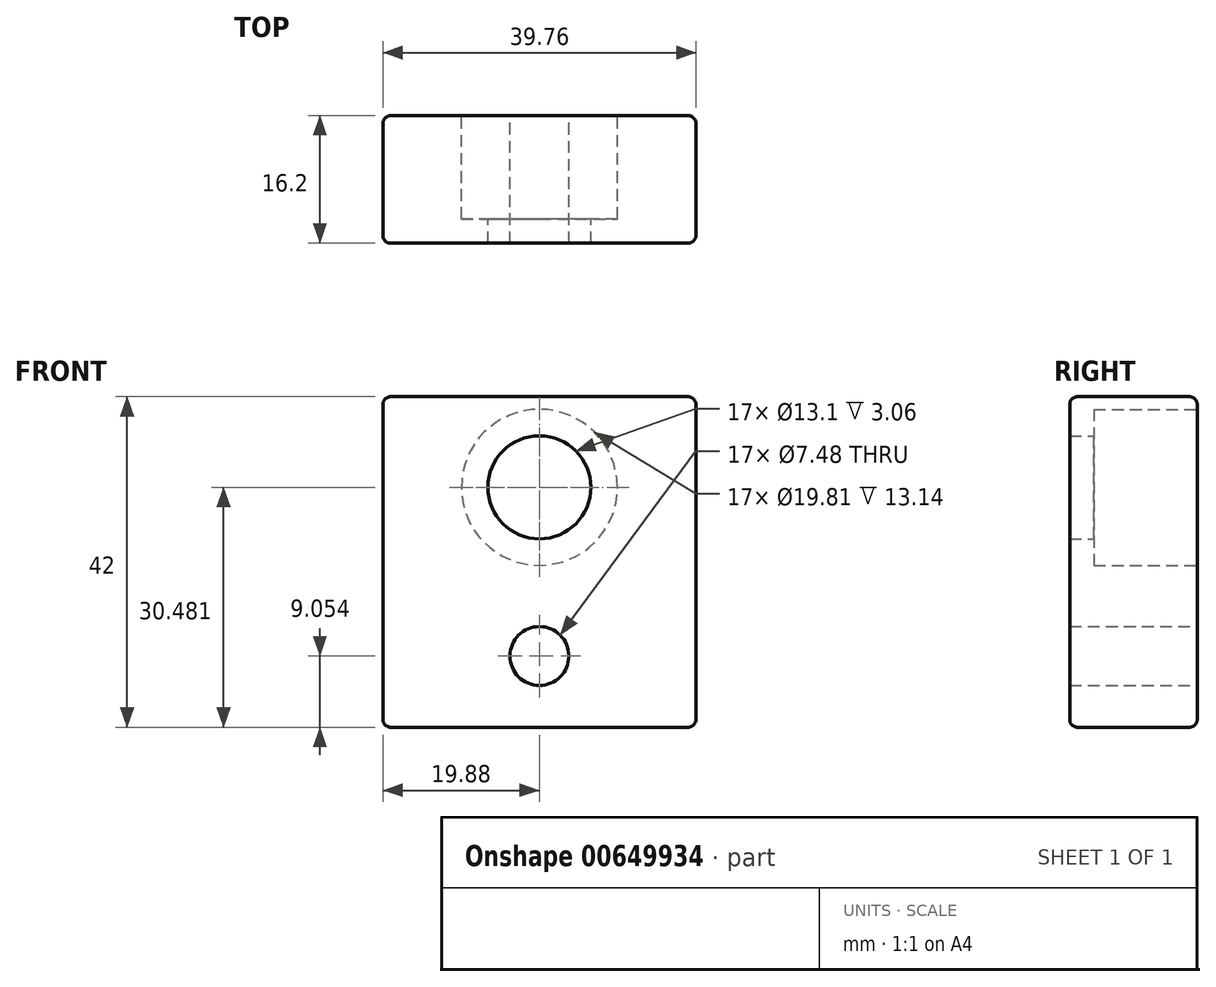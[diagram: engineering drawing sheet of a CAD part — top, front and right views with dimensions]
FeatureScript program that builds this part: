
annotation { "Feature Type Name" : "Feature", "Feature Type Description" : "" }
export const myFeature = defineFeature(function(context is Context, id is Id, definition is map)
    precondition{}
    {
        {
            var Q0;
            Q0=qCreatedBy(makeId("Front.planeOp"),FACE);
            var sketch = newSketch(context, id + "F0", { "sketchPlane" : qUnion([Q0])});
            skLineSegment(sketch, "E0.bottom", {"start": v(0, 0) * mm, "end": v(39.76, 0) * mm});
            skLineSegment(sketch, "E0.top", {"start": v(0, 42) * mm, "end": v(39.76, 42) * mm});
            skLineSegment(sketch, "E0.left", {"start": v(0, 0) * mm, "end": v(0, 42) * mm});
            skLineSegment(sketch, "E0.right", {"start": v(39.76, 0) * mm, "end": v(39.76, 42) * mm});
            skCircle(sketch, "E1", {"center": v(19.88, 9.05) * mm, "radius": 3.74 * mm});
            skPoint(sketch, "E2.centerSnap0", {"position": v(19.88, 42) * mm});
            skCircle(sketch, "E3", {"center": v(19.88, 30.48) * mm, "radius": 6.55 * mm});
            skSolve(sketch);
        }
        {
            var Q0;
            Q0=makeQuery(id+"F0.imprint","IMPRINT",FACE,{"disambiguationData":[TD([[makeQuery(id+"F0.imprint","IMPRINT",EDGE,{"derivedFrom":sQuery(id+"F0.wireOp",EDGE,"E0.bottom")}),1.0]])]});
            extrude(context, id + "F1", {"entities" : qUnion([Q0]), "endBound" : BoundingType.SYMMETRIC, "depth" : 16.2 * mm, "offsetDistance" : 25.4 * mm});
        }
        {
            var Q0;
            Q0=makeQuery(id+"F1.opExtrude","CAP_FACE",FACE,{"disambiguationData":[OSD([sQuery(id+"F0.wireOp",EDGE,"E0.bottom"),sQuery(id+"F0.wireOp",EDGE,"E0.top"),sQuery(id+"F0.wireOp",EDGE,"E0.left"),sQuery(id+"F0.wireOp",EDGE,"E0.right"),sQuery(id+"F0.wireOp",EDGE,"E1"),sQuery(id+"F0.wireOp",EDGE,"E3")])],"isStart":true});
            var sketch = newSketch(context, id + "F2", { "sketchPlane" : qUnion([Q0])});
            skCircle(sketch, "E4", {"center": v(-19.88, 30.48) * mm, "radius": 9.9 * mm});
            skSolve(sketch);
        }
        {
            var Q0;
            Q0=makeQuery(id+"F2.imprint","IMPRINT",FACE,{"disambiguationData":[TD([[makeQuery(id+"F2.imprint","IMPRINT",EDGE,{"derivedFrom":sQuery(id+"F2.wireOp",EDGE,"E4")}),1.0]])]});
            extrude(context, id + "F3", {"entities" : qUnion([Q0]), "operationType" : NewBodyOperationType.REMOVE, "oppositeDirection" : true, "depth" : 13.14 * mm, "offsetDistance" : 25.4 * mm});
        }
        {
            var Q0;
            Q0=makeQuery(id+"F1.opExtrude","CAP_EDGE",EDGE,{"disambiguationData":[OSD([sQuery(id+"F0.wireOp",EDGE,"E0.top")])],"isStart":false});
            var Q1;
            Q1=makeQuery(id+"F1.opExtrude","CAP_EDGE",EDGE,{"disambiguationData":[OSD([sQuery(id+"F0.wireOp",EDGE,"E0.right")])],"isStart":false});
            var Q2;
            Q2=makeQuery(id+"F1.opExtrude","CAP_EDGE",EDGE,{"disambiguationData":[OSD([sQuery(id+"F0.wireOp",EDGE,"E0.bottom")])],"isStart":false});
            var Q3;
            Q3=makeQuery(id+"F1.opExtrude","SWEPT_EDGE",EDGE,{"disambiguationData":[OSD([sQuery(id+"F0.wireOp",EDGE,"E0.top"),sQuery(id+"F0.wireOp",EDGE,"E0.right")])]});
            var Q4;
            Q4=makeQuery(id+"F1.opExtrude","SWEPT_EDGE",EDGE,{"disambiguationData":[OSD([sQuery(id+"F0.wireOp",EDGE,"E0.top"),sQuery(id+"F0.wireOp",EDGE,"E0.left")])]});
            var Q5;
            Q5=makeQuery(id+"F1.opExtrude","CAP_EDGE",EDGE,{"disambiguationData":[OSD([sQuery(id+"F0.wireOp",EDGE,"E0.top")])],"isStart":true});
            var Q6;
            Q6=makeQuery(id+"F1.opExtrude","CAP_EDGE",EDGE,{"disambiguationData":[OSD([sQuery(id+"F0.wireOp",EDGE,"E0.right")])],"isStart":true});
            var Q7;
            Q7=makeQuery(id+"F1.opExtrude","SWEPT_FACE",FACE,{"disambiguationData":[OSD([sQuery(id+"F0.wireOp",EDGE,"E0.right")])]});
            var Q8;
            Q8=makeQuery(id+"F1.opExtrude","CAP_EDGE",EDGE,{"disambiguationData":[OSD([sQuery(id+"F0.wireOp",EDGE,"E0.left")])],"isStart":false});
            var Q9;
            Q9=makeQuery(id+"F1.opExtrude","CAP_EDGE",EDGE,{"disambiguationData":[OSD([sQuery(id+"F0.wireOp",EDGE,"E0.left")])],"isStart":true});
            var Q10;
            Q10=makeQuery(id+"F1.opExtrude","CAP_EDGE",EDGE,{"disambiguationData":[OSD([sQuery(id+"F0.wireOp",EDGE,"E0.bottom")])],"isStart":true});
            var Q11;
            Q11=makeQuery(id+"F1.opExtrude","SWEPT_EDGE",EDGE,{"disambiguationData":[OSD([sQuery(id+"F0.wireOp",EDGE,"E0.bottom"),sQuery(id+"F0.wireOp",EDGE,"E0.left")])]});
            var Q12;
            Q12=makeQuery(id+"F1.opExtrude","SWEPT_EDGE",EDGE,{"disambiguationData":[OSD([sQuery(id+"F0.wireOp",EDGE,"E0.bottom"),sQuery(id+"F0.wireOp",EDGE,"E0.right")])]});
            fillet(context, id + "F4", {"entities" : qUnion([Q0, Q1, Q2, Q3, Q4, Q5, Q6, Q7, Q8, Q9, Q10, Q11, Q12]), "radius" : 1 * mm, "tangentPropagation" : true, "allowEdgeOverflow" : false});
        }
    });
